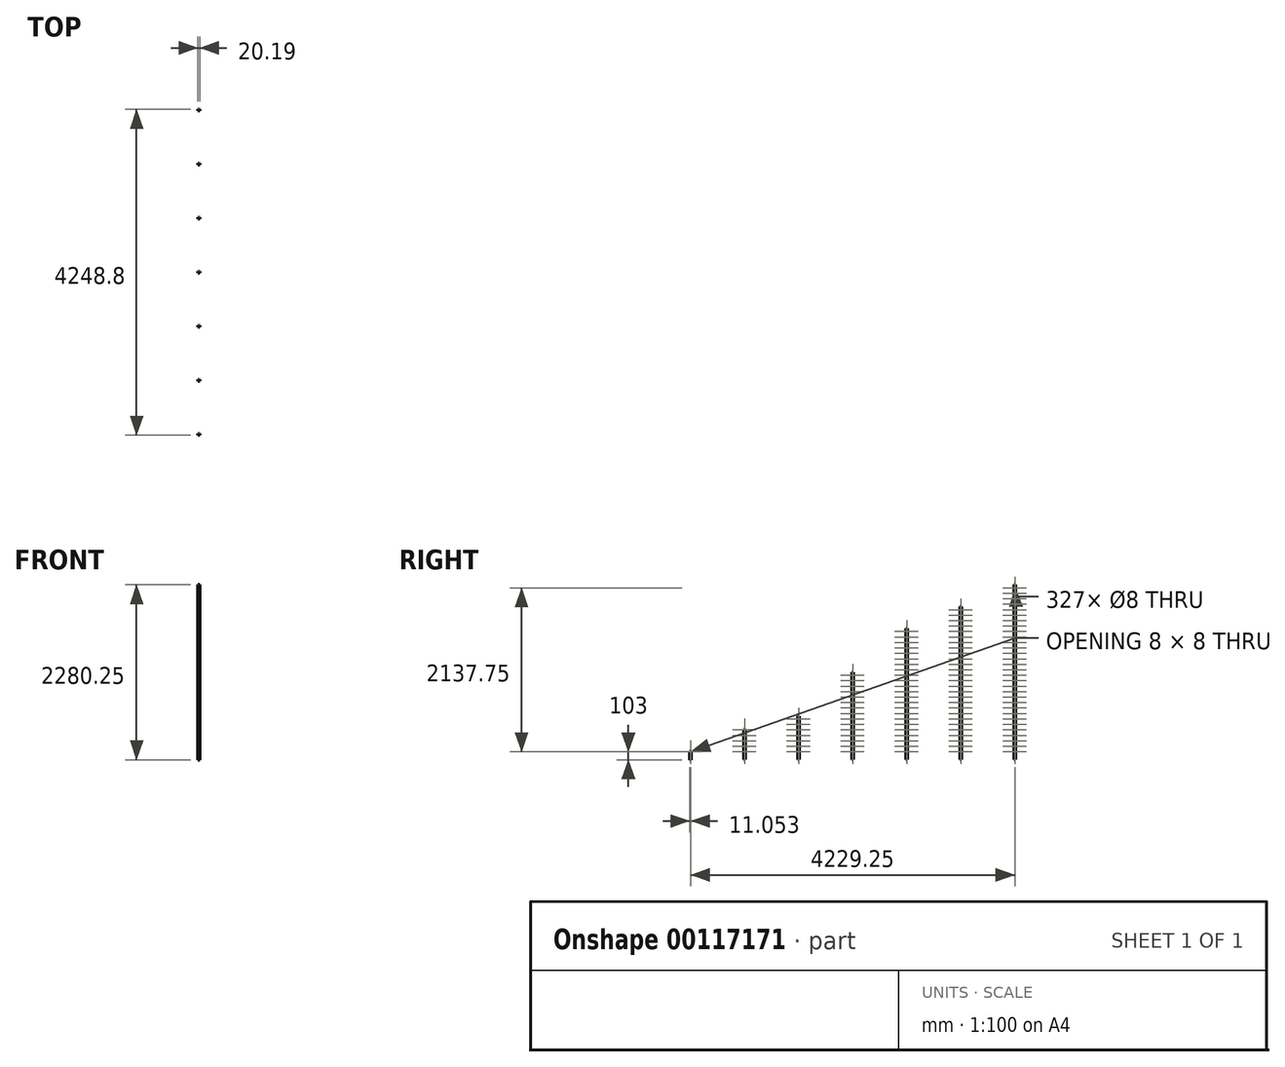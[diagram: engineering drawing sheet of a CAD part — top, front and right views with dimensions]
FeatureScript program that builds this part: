
annotation { "Feature Type Name" : "Feature", "Feature Type Description" : "" }
export const myFeature = defineFeature(function(context is Context, id is Id, definition is map)
    precondition{}
    {
        {
            var Q0;
            Q0=qCreatedBy(makeId("Right.planeOp"),FACE);
            var sketch = newSketch(context, id + "F0", { "sketchPlane" : qUnion([Q0])});
            skLineSegment(sketch, "E0", {"start": v(230.16, 1485) * mm, "end": v(211.16, 1485) * mm});
            skLineSegment(sketch, "E1", {"start": v(935.16, 1770) * mm, "end": v(916.16, 1770) * mm});
            skLineSegment(sketch, "E2", {"start": v(1640.16, 2055) * mm, "end": v(1621.16, 2055) * mm});
            skCircle(sketch, "E3", {"center": v(1631.66, 1730.5) * mm, "radius": 4 * mm});
            skCircle(sketch, "E4", {"center": v(1631.66, 1659.25) * mm, "radius": 4 * mm});
            skCircle(sketch, "E5", {"center": v(1631.66, 1588) * mm, "radius": 4 * mm});
            skCircle(sketch, "E6", {"center": v(1631.66, 1801.75) * mm, "radius": 4 * mm});
            skCircle(sketch, "E7", {"center": v(1631.66, 1944.25) * mm, "radius": 4 * mm});
            skCircle(sketch, "E8", {"center": v(221.66, 1445.5) * mm, "radius": 4 * mm});
            skCircle(sketch, "E9", {"center": v(1631.66, 1445.5) * mm, "radius": 4 * mm});
            skCircle(sketch, "E10", {"center": v(926.66, 1445.5) * mm, "radius": 4 * mm});
            skCircle(sketch, "E11", {"center": v(221.66, 1160.5) * mm, "radius": 4 * mm});
            skCircle(sketch, "E12", {"center": v(221.66, 1231.75) * mm, "radius": 4 * mm});
            skCircle(sketch, "E13", {"center": v(221.66, 1374.25) * mm, "radius": 4 * mm});
            skCircle(sketch, "E14", {"center": v(221.66, 1303) * mm, "radius": 4 * mm});
            skCircle(sketch, "E15", {"center": v(926.66, 1303) * mm, "radius": 4 * mm});
            skCircle(sketch, "E16", {"center": v(926.66, 1374.25) * mm, "radius": 4 * mm});
            skCircle(sketch, "E17", {"center": v(926.66, 1231.75) * mm, "radius": 4 * mm});
            skCircle(sketch, "E18", {"center": v(926.66, 1160.5) * mm, "radius": 4 * mm});
            skCircle(sketch, "E19", {"center": v(1631.66, 1160.5) * mm, "radius": 4 * mm});
            skCircle(sketch, "E20", {"center": v(1631.66, 1231.75) * mm, "radius": 4 * mm});
            skCircle(sketch, "E21", {"center": v(1631.66, 1374.25) * mm, "radius": 4 * mm});
            skCircle(sketch, "E22", {"center": v(1631.66, 1303) * mm, "radius": 4 * mm});
            skCircle(sketch, "E23", {"center": v(1631.66, 1873) * mm, "radius": 4 * mm});
            skCircle(sketch, "E24", {"center": v(1631.66, 2015.5) * mm, "radius": 4 * mm});
            skCircle(sketch, "E25", {"center": v(1631.66, 1516.75) * mm, "radius": 4 * mm});
            skCircle(sketch, "E26", {"center": v(926.66, 1730.5) * mm, "radius": 4 * mm});
            skCircle(sketch, "E27", {"center": v(1631.66, 661.75) * mm, "radius": 4 * mm});
            skCircle(sketch, "E28", {"center": v(221.66, 661.75) * mm, "radius": 4 * mm});
            skCircle(sketch, "E29", {"center": v(926.66, 661.75) * mm, "radius": 4 * mm});
            skCircle(sketch, "E30", {"center": v(926.66, 1588) * mm, "radius": 4 * mm});
            skCircle(sketch, "E31", {"center": v(926.66, 1659.25) * mm, "radius": 4 * mm});
            skCircle(sketch, "E32", {"center": v(926.66, 1516.75) * mm, "radius": 4 * mm});
            skCircle(sketch, "E33", {"center": v(1631.66, 234.25) * mm, "radius": 4 * mm});
            skCircle(sketch, "E34", {"center": v(221.66, 519.25) * mm, "radius": 4 * mm});
            skCircle(sketch, "E35", {"center": v(926.66, 519.25) * mm, "radius": 4 * mm});
            skCircle(sketch, "E36", {"center": v(926.66, 590.5) * mm, "radius": 4 * mm});
            skCircle(sketch, "E37", {"center": v(1631.66, 590.5) * mm, "radius": 4 * mm});
            skCircle(sketch, "E38", {"center": v(1631.66, 519.25) * mm, "radius": 4 * mm});
            skCircle(sketch, "E39", {"center": v(221.66, 91.75) * mm, "radius": 4 * mm});
            skCircle(sketch, "E40", {"center": v(221.66, 448) * mm, "radius": 4 * mm});
            skCircle(sketch, "E41", {"center": v(221.66, 376.75) * mm, "radius": 4 * mm});
            skCircle(sketch, "E42", {"center": v(221.66, 163) * mm, "radius": 4 * mm});
            skCircle(sketch, "E43", {"center": v(221.66, 305.5) * mm, "radius": 4 * mm});
            skCircle(sketch, "E44", {"center": v(221.66, 234.25) * mm, "radius": 4 * mm});
            skCircle(sketch, "E45", {"center": v(221.66, 590.5) * mm, "radius": 4 * mm});
            skCircle(sketch, "E46", {"center": v(926.66, 234.25) * mm, "radius": 4 * mm});
            skCircle(sketch, "E47", {"center": v(926.66, 305.5) * mm, "radius": 4 * mm});
            skCircle(sketch, "E48", {"center": v(926.66, 163) * mm, "radius": 4 * mm});
            skCircle(sketch, "E49", {"center": v(926.66, 376.75) * mm, "radius": 4 * mm});
            skCircle(sketch, "E50", {"center": v(926.66, 448) * mm, "radius": 4 * mm});
            skCircle(sketch, "E51", {"center": v(926.66, 91.75) * mm, "radius": 4 * mm});
            skCircle(sketch, "E52", {"center": v(1631.66, 91.75) * mm, "radius": 4 * mm});
            skCircle(sketch, "E53", {"center": v(1631.66, 448) * mm, "radius": 4 * mm});
            skCircle(sketch, "E54", {"center": v(1631.66, 376.75) * mm, "radius": 4 * mm});
            skCircle(sketch, "E55", {"center": v(1631.66, 163) * mm, "radius": 4 * mm});
            skCircle(sketch, "E56", {"center": v(1631.66, 305.5) * mm, "radius": 4 * mm});
            skCircle(sketch, "E57", {"center": v(926.66, 1018) * mm, "radius": 4 * mm});
            skCircle(sketch, "E58", {"center": v(1631.66, 1018) * mm, "radius": 4 * mm});
            skCircle(sketch, "E59", {"center": v(1631.66, 946.75) * mm, "radius": 4 * mm});
            skCircle(sketch, "E60", {"center": v(1631.66, 875.5) * mm, "radius": 4 * mm});
            skCircle(sketch, "E61", {"center": v(1631.66, 804.25) * mm, "radius": 4 * mm});
            skCircle(sketch, "E62", {"center": v(1631.66, 733) * mm, "radius": 4 * mm});
            skCircle(sketch, "E63", {"center": v(926.66, 733) * mm, "radius": 4 * mm});
            skCircle(sketch, "E64", {"center": v(221.66, 733) * mm, "radius": 4 * mm});
            skCircle(sketch, "E65", {"center": v(221.66, 946.75) * mm, "radius": 4 * mm});
            skCircle(sketch, "E66", {"center": v(221.66, 875.5) * mm, "radius": 4 * mm});
            skCircle(sketch, "E67", {"center": v(221.66, 804.25) * mm, "radius": 4 * mm});
            skCircle(sketch, "E68", {"center": v(221.66, 1018) * mm, "radius": 4 * mm});
            skCircle(sketch, "E69", {"center": v(926.66, 804.25) * mm, "radius": 4 * mm});
            skCircle(sketch, "E70", {"center": v(926.66, 875.5) * mm, "radius": 4 * mm});
            skCircle(sketch, "E71", {"center": v(926.66, 946.75) * mm, "radius": 4 * mm});
            skLineSegment(sketch, "E72", {"start": v(1640.16, -225) * mm, "end": v(1621.16, -225) * mm});
            skCircle(sketch, "E73", {"center": v(1631.66, -122) * mm, "radius": 4 * mm});
            skCircle(sketch, "E74", {"center": v(221.66, -50.75) * mm, "radius": 4 * mm});
            skCircle(sketch, "E75", {"center": v(221.66, -122) * mm, "radius": 4 * mm});
            skCircle(sketch, "E76", {"center": v(926.66, -122) * mm, "radius": 4 * mm});
            skCircle(sketch, "E77", {"center": v(926.66, -50.75) * mm, "radius": 4 * mm});
            skCircle(sketch, "E78", {"center": v(1631.66, -50.75) * mm, "radius": 4 * mm});
            skLineSegment(sketch, "E79", {"start": v(230.16, -225) * mm, "end": v(211.16, -225) * mm});
            skLineSegment(sketch, "E80", {"start": v(935.16, -225) * mm, "end": v(916.16, -225) * mm});
            skLineSegment(sketch, "E81", {"start": v(-1179.84, 345) * mm, "end": v(-1198.84, 345) * mm});
            skCircle(sketch, "E82", {"center": v(-483.34, 661.75) * mm, "radius": 4 * mm});
            skCircle(sketch, "E83", {"center": v(-1188.34, 91.75) * mm, "radius": 4 * mm});
            skCircle(sketch, "E84", {"center": v(-483.34, 448) * mm, "radius": 4 * mm});
            skCircle(sketch, "E85", {"center": v(-483.34, 519.25) * mm, "radius": 4 * mm});
            skCircle(sketch, "E86", {"center": v(-483.34, 590.5) * mm, "radius": 4 * mm});
            skCircle(sketch, "E87", {"center": v(-483.34, 163) * mm, "radius": 4 * mm});
            skCircle(sketch, "E88", {"center": v(-483.34, 234.25) * mm, "radius": 4 * mm});
            skCircle(sketch, "E89", {"center": v(-483.34, 91.75) * mm, "radius": 4 * mm});
            skCircle(sketch, "E90", {"center": v(-483.34, 305.5) * mm, "radius": 4 * mm});
            skCircle(sketch, "E91", {"center": v(-483.34, 376.75) * mm, "radius": 4 * mm});
            skCircle(sketch, "E92", {"center": v(-483.34, 875.5) * mm, "radius": 4 * mm});
            skCircle(sketch, "E93", {"center": v(-483.34, 733) * mm, "radius": 4 * mm});
            skCircle(sketch, "E94", {"center": v(-483.34, 804.25) * mm, "radius": 4 * mm});
            skLineSegment(sketch, "E95", {"start": v(-474.84, 915) * mm, "end": v(-493.84, 915) * mm});
            skCircle(sketch, "E96", {"center": v(-1188.34, 305.5) * mm, "radius": 4 * mm});
            skCircle(sketch, "E97", {"center": v(-1188.34, 234.25) * mm, "radius": 4 * mm});
            skCircle(sketch, "E98", {"center": v(-1188.34, 163) * mm, "radius": 4 * mm});
            skCircle(sketch, "E99", {"center": v(-1893.34, 91.75) * mm, "radius": 4 * mm});
            skCircle(sketch, "E100", {"center": v(-1893.34, 163) * mm, "radius": 4 * mm});
            skLineSegment(sketch, "E101", {"start": v(-1884.84, 170) * mm, "end": v(-1903.84, 170) * mm});
            skLineSegment(sketch, "E102", {"start": v(-1179.84, -225) * mm, "end": v(-1198.84, -225) * mm});
            skLineSegment(sketch, "E103", {"start": v(-474.84, -225) * mm, "end": v(-493.84, -225) * mm});
            skLineSegment(sketch, "E104", {"start": v(-1884.84, -225) * mm, "end": v(-1903.84, -225) * mm});
            skCircle(sketch, "E105", {"center": v(-1188.34, -50.75) * mm, "radius": 4 * mm});
            skCircle(sketch, "E106", {"center": v(-1188.34, -122) * mm, "radius": 4 * mm});
            skCircle(sketch, "E107", {"center": v(-483.34, -50.75) * mm, "radius": 4 * mm});
            skCircle(sketch, "E108", {"center": v(-483.34, -122) * mm, "radius": 4 * mm});
            skCircle(sketch, "E109", {"center": v(-2597.59, -122.25) * mm, "radius": 4 * mm});
            skLineSegment(sketch, "E110", {"start": v(-2589.64, -115.25) * mm, "end": v(-2608.64, -115.25) * mm});
            skLineSegment(sketch, "E111", {"start": v(-2608.64, -225) * mm, "end": v(-2608.64, -201) * mm});
            skLineSegment(sketch, "E112", {"start": v(-2589.64, -225.25) * mm, "end": v(-2608.64, -225.25) * mm});
            skLineSegment(sketch, "E113", {"start": v(-2608.64, -225) * mm, "end": v(-2608.84, -225) * mm});
            skLineSegment(sketch, "E114", {"start": v(-2589.64, -225.25) * mm, "end": v(-2589.64, -115.25) * mm});
            skLineSegment(sketch, "E115", {"start": v(-2608.64, -225.25) * mm, "end": v(-2608.64, -115.25) * mm});
            skCircle(sketch, "E116", {"center": v(926.66, 1089.25) * mm, "radius": 4 * mm});
            skCircle(sketch, "E117", {"center": v(1631.66, 1089.25) * mm, "radius": 4 * mm});
            skCircle(sketch, "E118", {"center": v(221.66, 1089.25) * mm, "radius": 4 * mm});
            skCircle(sketch, "E119", {"center": v(-1893.34, -122) * mm, "radius": 4 * mm});
            skCircle(sketch, "E120", {"center": v(-1893.34, -50.75) * mm, "radius": 4 * mm});
            skLineSegment(sketch, "E121", {"start": v(1640.16, -225) * mm, "end": v(1640.16, 2055) * mm});
            skLineSegment(sketch, "E122", {"start": v(1621.16, -225) * mm, "end": v(1621.16, 2055) * mm});
            skLineSegment(sketch, "E123", {"start": v(211.16, -225) * mm, "end": v(211.16, 1485) * mm});
            skLineSegment(sketch, "E124", {"start": v(230.16, -225) * mm, "end": v(230.16, 1485) * mm});
            skLineSegment(sketch, "E125", {"start": v(916.16, -225) * mm, "end": v(916.16, 1770) * mm});
            skLineSegment(sketch, "E126", {"start": v(935.16, -225) * mm, "end": v(935.16, 1770) * mm});
            skLineSegment(sketch, "E127", {"start": v(-493.84, -225) * mm, "end": v(-493.84, 915) * mm});
            skLineSegment(sketch, "E128", {"start": v(-474.84, -225) * mm, "end": v(-474.84, 915) * mm});
            skCircle(sketch, "E129", {"center": v(1631.66, 20.5) * mm, "radius": 4 * mm});
            skCircle(sketch, "E130", {"center": v(221.66, 20.5) * mm, "radius": 4 * mm});
            skCircle(sketch, "E131", {"center": v(926.66, 20.5) * mm, "radius": 4 * mm});
            skCircle(sketch, "E132", {"center": v(-1188.34, 20.5) * mm, "radius": 4 * mm});
            skCircle(sketch, "E133", {"center": v(-483.34, 20.5) * mm, "radius": 4 * mm});
            skCircle(sketch, "E134", {"center": v(-1893.34, 20.5) * mm, "radius": 4 * mm});
            skLineSegment(sketch, "E135", {"start": v(-1903.84, -225) * mm, "end": v(-1903.84, 170) * mm});
            skLineSegment(sketch, "E136", {"start": v(-1884.84, -225) * mm, "end": v(-1884.84, 170) * mm});
            skLineSegment(sketch, "E137", {"start": v(-1198.84, -225) * mm, "end": v(-1198.84, 345) * mm});
            skLineSegment(sketch, "E138", {"start": v(-1179.84, -225) * mm, "end": v(-1179.84, 345) * mm});
            skSolve(sketch);
        }
        {
            var Q0;
            Q0 = qSketchRegion(id + "F0", true);
            extrude(context, id + "F1", {"entities" : qUnion([Q0]), "depth" : 20.2 * mm});
        }
        {
            var Q0;
            Q0=makeQuery(id+"F1.opExtrude","SWEPT_FACE",FACE,{"disambiguationData":[OSD([sQuery(id+"F0.wireOp",EDGE,"E112")])]});
            var sketch = newSketch(context, id + "F2", { "sketchPlane" : qUnion([Q0])});
            skLineSegment(sketch, "E139", {"start": v(9, 2606.64) * mm, "end": v(2, 2606.64) * mm});
            skLineSegment(sketch, "E140", {"start": v(18.2, 2606.64) * mm, "end": v(11.2, 2606.64) * mm});
            skLineSegment(sketch, "E141", {"start": v(9, 2606.64) * mm, "end": v(9, 2589.64) * mm});
            skLineSegment(sketch, "E142", {"start": v(18.2, 2606.64) * mm, "end": v(18.2, 2589.64) * mm});
            skLineSegment(sketch, "E143", {"start": v(11.2, 2606.64) * mm, "end": v(11.2, 2589.64) * mm});
            skLineSegment(sketch, "E144", {"start": v(2, 2606.64) * mm, "end": v(2, 2589.64) * mm});
            skLineSegment(sketch, "E145", {"start": v(20.2, 2608.64) * mm, "end": v(0, 2608.64) * mm});
            skLineSegment(sketch, "E146", {"start": v(2, 2589.64) * mm, "end": v(9, 2589.64) * mm});
            skLineSegment(sketch, "E147", {"start": v(11.2, 2589.64) * mm, "end": v(18.2, 2589.64) * mm});
            skLineSegment(sketch, "E148", {"start": v(2, 2589.64) * mm, "end": v(0, 2589.64) * mm, "construction": true});
            skSolve(sketch);
        }
        {
            var Q0;
            Q0 = qSketchRegion(id + "F2", true);
            extrude(context, id + "F3", {"entities" : qUnion([Q0]), "operationType" : NewBodyOperationType.REMOVE, "endBound" : BoundingType.THROUGH_ALL, "oppositeDirection" : true, "depth" : 25.4 * mm});
        }
        {
            var Q0;
            Q0=makeQuery(id+"F1.opExtrude","SWEPT_FACE",FACE,{"disambiguationData":[OSD([sQuery(id+"F0.wireOp",EDGE,"E104")])]});
            var sketch = newSketch(context, id + "F4", { "sketchPlane" : qUnion([Q0])});
            skLineSegment(sketch, "E149", {"start": v(9.04, 1901.84) * mm, "end": v(2, 1901.84) * mm});
            skLineSegment(sketch, "E150", {"start": v(18.2, 1901.84) * mm, "end": v(11.2, 1901.84) * mm});
            skLineSegment(sketch, "E151", {"start": v(9.04, 1901.84) * mm, "end": v(9.04, 1884.84) * mm});
            skLineSegment(sketch, "E152", {"start": v(18.2, 1901.84) * mm, "end": v(18.2, 1884.84) * mm});
            skLineSegment(sketch, "E153", {"start": v(11.2, 1901.84) * mm, "end": v(11.2, 1884.84) * mm});
            skLineSegment(sketch, "E154", {"start": v(2, 1901.84) * mm, "end": v(2, 1884.84) * mm});
            skLineSegment(sketch, "E155", {"start": v(2, 1884.84) * mm, "end": v(9.04, 1884.84) * mm});
            skLineSegment(sketch, "E156", {"start": v(11.2, 1884.84) * mm, "end": v(18.2, 1884.84) * mm});
            skLineSegment(sketch, "E157", {"start": v(2, 1884.84) * mm, "end": v(0, 1884.84) * mm, "construction": true});
            skSolve(sketch);
        }
        {
            var Q0;
            Q0 = qSketchRegion(id + "F4", true);
            extrude(context, id + "F5", {"entities" : qUnion([Q0]), "operationType" : NewBodyOperationType.REMOVE, "endBound" : BoundingType.THROUGH_ALL, "oppositeDirection" : true, "depth" : 25.4 * mm});
        }
        {
            var Q0;
            Q0=makeQuery(id+"F1.opExtrude","SWEPT_FACE",FACE,{"disambiguationData":[OSD([sQuery(id+"F0.wireOp",EDGE,"E102")])]});
            var sketch = newSketch(context, id + "F6", { "sketchPlane" : qUnion([Q0])});
            skLineSegment(sketch, "E158", {"start": v(9, 1196.84) * mm, "end": v(2, 1196.84) * mm});
            skLineSegment(sketch, "E159", {"start": v(18.2, 1196.84) * mm, "end": v(11.2, 1196.84) * mm});
            skLineSegment(sketch, "E160", {"start": v(9, 1196.84) * mm, "end": v(9, 1179.84) * mm});
            skLineSegment(sketch, "E161", {"start": v(18.2, 1196.84) * mm, "end": v(18.2, 1179.84) * mm});
            skLineSegment(sketch, "E162", {"start": v(11.2, 1196.84) * mm, "end": v(11.2, 1179.84) * mm});
            skLineSegment(sketch, "E163", {"start": v(2, 1196.84) * mm, "end": v(2, 1179.84) * mm});
            skLineSegment(sketch, "E164", {"start": v(2, 1179.84) * mm, "end": v(9, 1179.84) * mm});
            skLineSegment(sketch, "E165", {"start": v(11.2, 1179.84) * mm, "end": v(18.2, 1179.84) * mm});
            skLineSegment(sketch, "E166", {"start": v(2, 1179.84) * mm, "end": v(0, 1179.84) * mm, "construction": true});
            skSolve(sketch);
        }
        {
            var Q0;
            Q0 = qSketchRegion(id + "F6", true);
            extrude(context, id + "F7", {"entities" : qUnion([Q0]), "operationType" : NewBodyOperationType.REMOVE, "endBound" : BoundingType.THROUGH_ALL, "oppositeDirection" : true, "depth" : 25.4 * mm});
        }
        {
            var Q0;
            Q0=makeQuery(id+"F1.opExtrude","SWEPT_FACE",FACE,{"disambiguationData":[OSD([sQuery(id+"F0.wireOp",EDGE,"E103")])]});
            var sketch = newSketch(context, id + "F8", { "sketchPlane" : qUnion([Q0])});
            skLineSegment(sketch, "E167", {"start": v(9, 491.84) * mm, "end": v(2, 491.84) * mm});
            skLineSegment(sketch, "E168", {"start": v(18.2, 491.84) * mm, "end": v(11.2, 491.84) * mm});
            skLineSegment(sketch, "E169", {"start": v(9, 491.84) * mm, "end": v(9, 474.84) * mm});
            skLineSegment(sketch, "E170", {"start": v(18.2, 491.84) * mm, "end": v(18.2, 474.84) * mm});
            skLineSegment(sketch, "E171", {"start": v(11.2, 491.84) * mm, "end": v(11.2, 474.84) * mm});
            skLineSegment(sketch, "E172", {"start": v(2, 491.84) * mm, "end": v(2, 474.84) * mm});
            skLineSegment(sketch, "E173", {"start": v(2, 474.84) * mm, "end": v(9, 474.84) * mm});
            skLineSegment(sketch, "E174", {"start": v(11.2, 474.84) * mm, "end": v(18.2, 474.84) * mm});
            skLineSegment(sketch, "E175", {"start": v(2, 474.84) * mm, "end": v(0, 474.84) * mm, "construction": true});
            skSolve(sketch);
        }
        {
            var Q0;
            Q0 = qSketchRegion(id + "F8", true);
            extrude(context, id + "F9", {"entities" : qUnion([Q0]), "operationType" : NewBodyOperationType.REMOVE, "endBound" : BoundingType.THROUGH_ALL, "oppositeDirection" : true, "depth" : 25.4 * mm});
        }
        {
            var Q0;
            Q0=makeQuery(id+"F1.opExtrude","SWEPT_FACE",FACE,{"disambiguationData":[OSD([sQuery(id+"F0.wireOp",EDGE,"E79")])]});
            var sketch = newSketch(context, id + "F10", { "sketchPlane" : qUnion([Q0])});
            skSolve(sketch);
        }
        {
            var Q0;
            {var subQ0=sQuery(id+"F0.wireOp",EDGE,"E79");Q0=makeQuery(id+"F10.imprint","IMPRINT",FACE,{"disambiguationData":[TD([[makeQuery(id+"F10.imprint","IMPRINT",EDGE,{"derivedFrom":makeQuery(id+"F1.opExtrude","CAP_EDGE",EDGE,{"disambiguationData":[OSD([subQ0])],"isStart":true})}),-1.0]])]});}
            var sketch = newSketch(context, id + "F11", { "sketchPlane" : qUnion([Q0])});
            skLineSegment(sketch, "E176", {"start": v(9.04, -213.16) * mm, "end": v(2, -213.16) * mm});
            skLineSegment(sketch, "E177", {"start": v(18.2, -213.16) * mm, "end": v(11.2, -213.16) * mm});
            skLineSegment(sketch, "E178", {"start": v(9.04, -213.16) * mm, "end": v(9.04, -230.16) * mm});
            skLineSegment(sketch, "E179", {"start": v(18.2, -213.16) * mm, "end": v(18.2, -230.16) * mm});
            skLineSegment(sketch, "E180", {"start": v(11.2, -213.16) * mm, "end": v(11.2, -230.16) * mm});
            skLineSegment(sketch, "E181", {"start": v(2, -213.16) * mm, "end": v(2, -230.16) * mm});
            skLineSegment(sketch, "E182", {"start": v(2, -230.16) * mm, "end": v(9.04, -230.16) * mm});
            skLineSegment(sketch, "E183", {"start": v(11.2, -230.16) * mm, "end": v(18.2, -230.16) * mm});
            skLineSegment(sketch, "E184", {"start": v(2, -230.16) * mm, "end": v(0, -230.16) * mm, "construction": true});
            skSolve(sketch);
        }
        {
            var Q0;
            Q0 = qSketchRegion(id + "F11", true);
            extrude(context, id + "F12", {"entities" : qUnion([Q0]), "operationType" : NewBodyOperationType.REMOVE, "endBound" : BoundingType.THROUGH_ALL, "oppositeDirection" : true, "depth" : 25.4 * mm});
        }
        {
            var Q0;
            Q0=makeQuery(id+"F1.opExtrude","SWEPT_FACE",FACE,{"disambiguationData":[OSD([sQuery(id+"F0.wireOp",EDGE,"E80")])]});
            var sketch = newSketch(context, id + "F13", { "sketchPlane" : qUnion([Q0])});
            skLineSegment(sketch, "E185", {"start": v(9.04, -918.16) * mm, "end": v(2, -918.16) * mm});
            skLineSegment(sketch, "E186", {"start": v(18.2, -918.16) * mm, "end": v(11.2, -918.16) * mm});
            skLineSegment(sketch, "E187", {"start": v(9.04, -918.16) * mm, "end": v(9.04, -935.16) * mm});
            skLineSegment(sketch, "E188", {"start": v(18.2, -918.16) * mm, "end": v(18.2, -935.16) * mm});
            skLineSegment(sketch, "E189", {"start": v(11.2, -918.16) * mm, "end": v(11.2, -935.16) * mm});
            skLineSegment(sketch, "E190", {"start": v(2, -918.16) * mm, "end": v(2, -935.16) * mm});
            skLineSegment(sketch, "E191", {"start": v(2, -935.16) * mm, "end": v(9.04, -935.16) * mm});
            skLineSegment(sketch, "E192", {"start": v(11.2, -935.16) * mm, "end": v(18.2, -935.16) * mm});
            skLineSegment(sketch, "E193", {"start": v(2, -935.16) * mm, "end": v(0, -935.16) * mm, "construction": true});
            skSolve(sketch);
        }
        {
            var Q0;
            Q0 = qSketchRegion(id + "F13", true);
            extrude(context, id + "F14", {"entities" : qUnion([Q0]), "operationType" : NewBodyOperationType.REMOVE, "endBound" : BoundingType.THROUGH_ALL, "oppositeDirection" : true, "depth" : 25.4 * mm});
        }
        {
            var Q0;
            Q0=makeQuery(id+"F1.opExtrude","SWEPT_FACE",FACE,{"disambiguationData":[OSD([sQuery(id+"F0.wireOp",EDGE,"E72")])]});
            var sketch = newSketch(context, id + "F15", { "sketchPlane" : qUnion([Q0])});
            skLineSegment(sketch, "E194", {"start": v(9.04, -1623.16) * mm, "end": v(2, -1623.16) * mm});
            skLineSegment(sketch, "E195", {"start": v(18.2, -1623.16) * mm, "end": v(11.2, -1623.16) * mm});
            skLineSegment(sketch, "E196", {"start": v(9.04, -1623.16) * mm, "end": v(9.04, -1640.16) * mm});
            skLineSegment(sketch, "E197", {"start": v(18.2, -1623.16) * mm, "end": v(18.2, -1640.16) * mm});
            skLineSegment(sketch, "E198", {"start": v(11.2, -1623.16) * mm, "end": v(11.2, -1640.16) * mm});
            skLineSegment(sketch, "E199", {"start": v(2, -1623.16) * mm, "end": v(2, -1640.16) * mm});
            skLineSegment(sketch, "E200", {"start": v(2, -1640.16) * mm, "end": v(9.04, -1640.16) * mm});
            skLineSegment(sketch, "E201", {"start": v(11.2, -1640.16) * mm, "end": v(18.2, -1640.16) * mm});
            skLineSegment(sketch, "E202", {"start": v(2, -1640.16) * mm, "end": v(0, -1640.16) * mm, "construction": true});
            skSolve(sketch);
        }
        {
            var Q0;
            Q0 = qSketchRegion(id + "F15", true);
            extrude(context, id + "F16", {"entities" : qUnion([Q0]), "operationType" : NewBodyOperationType.REMOVE, "endBound" : BoundingType.THROUGH_ALL, "oppositeDirection" : true, "depth" : 25.4 * mm});
        }
    });
